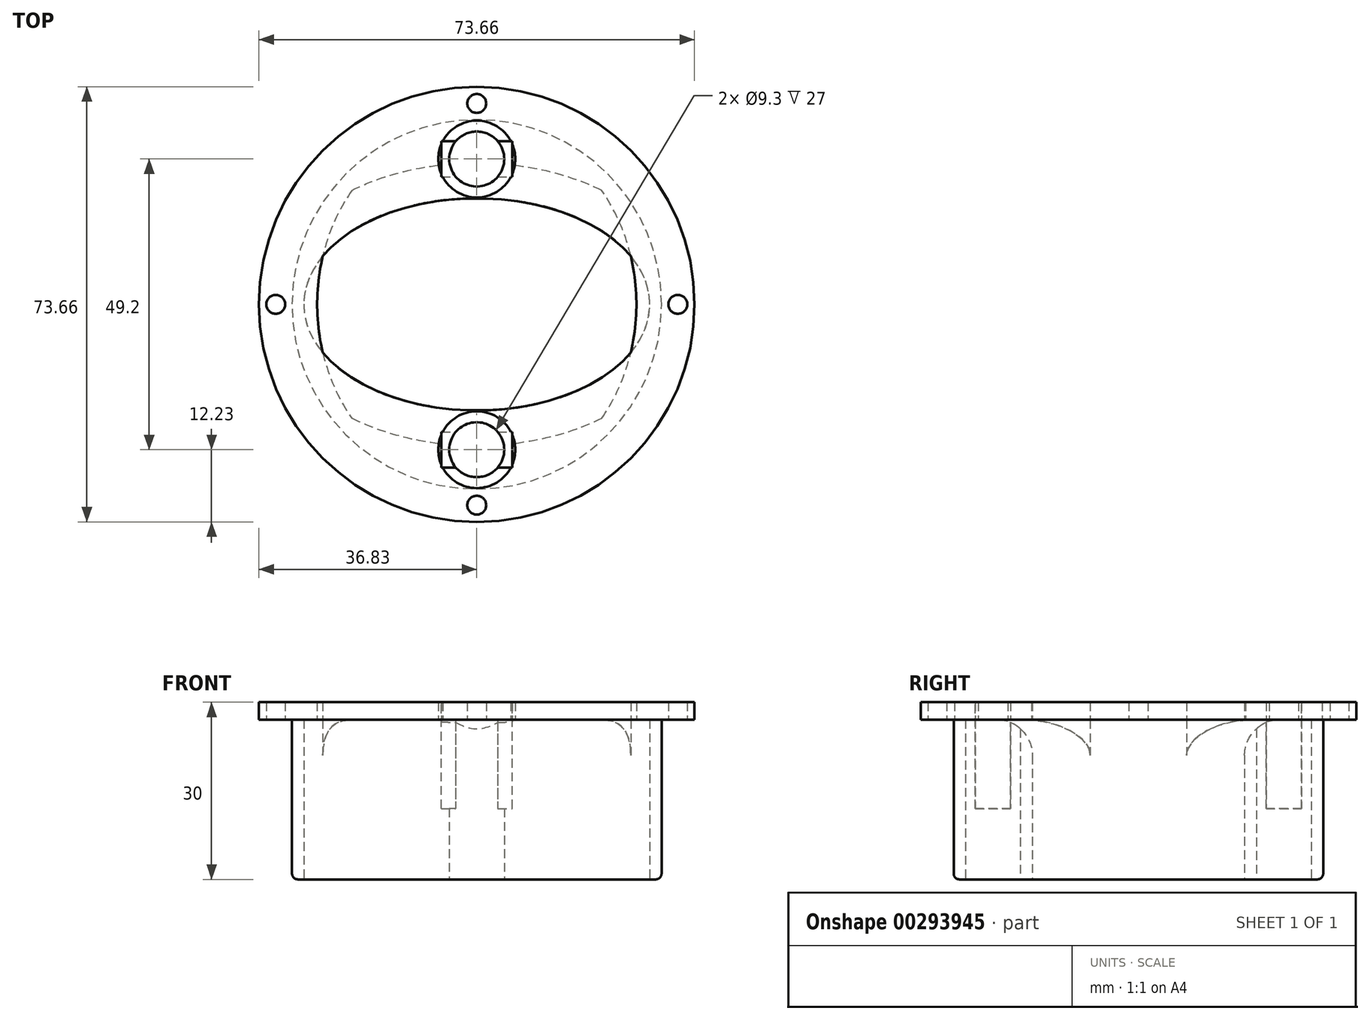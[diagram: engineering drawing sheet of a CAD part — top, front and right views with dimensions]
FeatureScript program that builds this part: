
annotation { "Feature Type Name" : "Feature", "Feature Type Description" : "" }
export const myFeature = defineFeature(function(context is Context, id is Id, definition is map)
    precondition{}
    {
        {
            var Q0;
            Q0=qCreatedBy(makeId("Top.planeOp"),FACE);
            var sketch = newSketch(context, id + "F0", { "sketchPlane" : qUnion([Q0])});
            skCircle(sketch, "E0", {"center": v(0, 0) * mm, "radius": 31.25 * mm});
            skCircle(sketch, "E1", {"center": v(0, 24.6) * mm, "radius": 4.65 * mm});
            skLineSegment(sketch, "E2", {"start": v(-31.25, 0) * mm, "end": v(31.25, 0) * mm, "construction": true});
            skCircle(sketch, "E3.MirrorC", {"center": v(0, -24.6) * mm, "radius": 4.65 * mm});
            skEllipse(sketch, "E4", {"center": v(0, 0) * mm, "majorRadius": 29.25 * mm, "minorRadius": 17.95 * mm, "majorAxis": v(-1, 0)});
            skPoint(sketch, "E5", {"position": v(0, 17.95) * mm});
            skPoint(sketch, "E6", {"position": v(0, -17.95) * mm});
            skPoint(sketch, "E7", {"position": v(29.25, 0) * mm});
            skSolve(sketch);
        }
        {
            var Q0;
            Q0 = qSketchRegion(id + "F0", true);
            extrude(context, id + "F1", {"entities" : qUnion([Q0]), "depth" : 27 * mm, "offsetDistance" : 25 * mm});
        }
        {
            var Q0;
            Q0=makeQuery(id+"F1.opExtrude","CAP_FACE",FACE,{"disambiguationData":[OSD([sQuery(id+"F0.wireOp",EDGE,"E0"),sQuery(id+"F0.wireOp",EDGE,"E1"),sQuery(id+"F0.wireOp",EDGE,"E3.MirrorC"),sQuery(id+"F0.wireOp",EDGE,"E4")])],"isStart":false});
            var sketch = newSketch(context, id + "F2", { "sketchPlane" : qUnion([Q0])});
            skCircle(sketch, "E8", {"center": v(0, 0) * mm, "radius": 36.83 * mm});
            skCircle(sketch, "E9", {"center": v(0, 34) * mm, "radius": 1.6 * mm});
            skCircle(sketch, "E10.1.0", {"center": v(-34, 0) * mm, "radius": 1.6 * mm});
            skCircle(sketch, "E10.2.0", {"center": v(0, -34) * mm, "radius": 1.6 * mm});
            skCircle(sketch, "E10.3.0", {"center": v(34, 0) * mm, "radius": 1.6 * mm});
            skEllipse(sketch, "E11", {"center": v(0, 0) * mm, "majorRadius": 31 * mm, "minorRadius": 27 * mm, "majorAxis": v(0, 1)});
            skPoint(sketch, "E12", {"position": v(-27, 0) * mm});
            skPoint(sketch, "E13", {"position": v(27, 0) * mm});
            skSolve(sketch);
        }
        {
            var Q0;
            Q0 = qSketchRegion(id + "F2", true);
            extrude(context, id + "F3", {"entities" : qUnion([Q0]), "operationType" : NewBodyOperationType.ADD, "depth" : 3 * mm, "offsetDistance" : 25 * mm});
        }
        {
            var Q0;
            {var subQ0=sQuery(id+"F0.wireOp",EDGE,"E4");Q0=makeQuery(id+"F3.boolean.opBoolean","SPLIT",EDGE,{"disambiguationData":[topologyDisambiguationEdgeConnected([makeQuery(id+"F1.opExtrude","SWEPT_FACE",FACE,{"disambiguationData":[OSD([subQ0])]}),makeQuery(id+"F3.opExtrude","CAP_FACE",FACE,{"disambiguationData":[OSD([sQuery(id+"F2.wireOp",EDGE,"E8"),sQuery(id+"F2.wireOp",EDGE,"E9"),sQuery(id+"F2.wireOp",EDGE,"E10.1.0"),sQuery(id+"F2.wireOp",EDGE,"E10.2.0"),sQuery(id+"F2.wireOp",EDGE,"E10.3.0"),sQuery(id+"F2.wireOp",EDGE,"E11")])],"isStart":true})]),OD(0.0)],"derivedFrom":makeQuery(id+"F1.opExtrude","CAP_EDGE",EDGE,{"disambiguationData":[OSD([subQ0])],"isStart":false})});}
            var Q1;
            {var subQ0=sQuery(id+"F0.wireOp",EDGE,"E4");Q1=makeQuery(id+"F3.boolean.opBoolean","SPLIT",EDGE,{"disambiguationData":[topologyDisambiguationEdgeConnected([makeQuery(id+"F1.opExtrude","SWEPT_FACE",FACE,{"disambiguationData":[OSD([subQ0])]}),makeQuery(id+"F3.opExtrude","CAP_FACE",FACE,{"disambiguationData":[OSD([sQuery(id+"F2.wireOp",EDGE,"E8"),sQuery(id+"F2.wireOp",EDGE,"E9"),sQuery(id+"F2.wireOp",EDGE,"E10.1.0"),sQuery(id+"F2.wireOp",EDGE,"E10.2.0"),sQuery(id+"F2.wireOp",EDGE,"E10.3.0"),sQuery(id+"F2.wireOp",EDGE,"E11")])],"isStart":true})]),OD(1.0)],"derivedFrom":makeQuery(id+"F1.opExtrude","CAP_EDGE",EDGE,{"disambiguationData":[OSD([subQ0])],"isStart":false})});}
            fillet(context, id + "F4", {"entities" : qUnion([Q0, Q1]), "tangentPropagation" : true, "radius" : 6 * mm, "defaultsChanged" : true, "vertexSettings" : [], "allowEdgeOverflow" : false});
        }
        {
            var Q0;
            {var subQ0=sQuery(id+"F0.wireOp",EDGE,"E3.MirrorC");var subQ2=sQuery(id+"F0.wireOp",EDGE,"E4");Q0=makeQuery(id+"F3.boolean.opBoolean","SPLIT",FACE,{"disambiguationData":[TD([makeQuery(id+"F1.opExtrude","SWEPT_FACE",FACE,{"disambiguationData":[OSD([subQ0])]})])],"derivedFrom":makeQuery(id+"F1.opExtrude","CAP_FACE",FACE,{"disambiguationData":[OSD([sQuery(id+"F0.wireOp",EDGE,"E0"),sQuery(id+"F0.wireOp",EDGE,"E1"),subQ0,subQ2])],"isStart":false})});}
            var sketch = newSketch(context, id + "F5", { "sketchPlane" : qUnion([Q0])});
            skEllipticalArc(sketch, "E14.0", {});
            skEllipticalArc(sketch, "E14.1", {});
            skEllipticalArc(sketch, "E14.2", {});
            skCircle(sketch, "E15", {"center": v(0, 24.6) * mm, "radius": 6.4 * mm});
            skCircle(sketch, "E16", {"center": v(0, -24.6) * mm, "radius": 6.4 * mm});
            skEllipticalArc(sketch, "E17.trimOffspring", {});
            const initialGuessF5  = {"E14.0": [0, 0, -1, 0, 0.02925, 0.01795, 0.4724535712676554, 2.669139082322136], "E14.1": [0, 0, 0, 1, 0.031, 0.027, 1.8374466509007625, 4.445738656278822], "E14.2": [0, 0, -1, 0, 0.02925, 0.01795, 3.614046224857449, 5.810731735911931], "E17.trimOffspring": [0, 0, 0, 1, 0.031, 0.027, 4.979039304490556, 1.3041460026890304]};
            skSetInitialGuess(sketch, initialGuessF5);
            skSolve(sketch);
        }
        {
            var Q0;
            Q0 = qSketchRegion(id + "F5", true);
            var Q1;
            Q1=makeQuery(id+"F3.opExtrude","CAP_FACE",FACE,{"disambiguationData":[OSD([sQuery(id+"F2.wireOp",EDGE,"E8"),sQuery(id+"F2.wireOp",EDGE,"E9"),sQuery(id+"F2.wireOp",EDGE,"E10.1.0"),sQuery(id+"F2.wireOp",EDGE,"E10.2.0"),sQuery(id+"F2.wireOp",EDGE,"E10.3.0"),sQuery(id+"F2.wireOp",EDGE,"E11")])],"isStart":false});
            extrude(context, id + "F6", {"entities" : qUnion([Q0]), "operationType" : NewBodyOperationType.ADD, "endBound" : BoundingType.UP_TO_SURFACE, "depth" : 25 * mm, "endBoundEntityFace" : qUnion([Q1]), "offsetDistance" : 25 * mm});
        }
        {
            var Q0;
            Q0=makeQuery(id+"F6.opExtrude","CAP_FACE",FACE,{"disambiguationData":[OSD([sQuery(id+"F5.wireOp",EDGE,"E14.2"),sQuery(id+"F5.wireOp",EDGE,"E17.trimOffspring")])],"isStart":true});
            var sketch = newSketch(context, id + "F7", { "sketchPlane" : qUnion([Q0])});
            skCircle(sketch, "E18", {"center": v(0, 24.6) * mm, "radius": 6.5 * mm});
            skCircle(sketch, "E19", {"center": v(0, -24.6) * mm, "radius": 6.5 * mm});
            skSolve(sketch);
        }
        {
            var Q0;
            Q0 = qSketchRegion(id + "F7", true);
            extrude(context, id + "F8", {"entities" : qUnion([Q0]), "operationType" : NewBodyOperationType.REMOVE, "endBound" : BoundingType.THROUGH_ALL, "oppositeDirection" : true, "depth" : 25 * mm, "offsetDistance" : 25 * mm});
        }
        {
            var Q0;
            Q0=makeQuery(id+"F1.opExtrude","CAP_EDGE",EDGE,{"disambiguationData":[OSD([sQuery(id+"F0.wireOp",EDGE,"E0")])],"isStart":true});
            fillet(context, id + "F9", {"entities" : qUnion([Q0]), "tangentPropagation" : true, "radius" : 1 * mm, "defaultsChanged" : true, "vertexSettings" : [], "allowEdgeOverflow" : false});
        }
        {
            var Q0;
            Q0=makeQuery(id+"F6.boolean.opBoolean","MERGE",FACE,{"derivedFrom":[makeQuery(id+"F3.opExtrude","CAP_FACE",FACE,{"disambiguationData":[OSD([sQuery(id+"F2.wireOp",EDGE,"E8"),sQuery(id+"F2.wireOp",EDGE,"E9"),sQuery(id+"F2.wireOp",EDGE,"E10.1.0"),sQuery(id+"F2.wireOp",EDGE,"E10.2.0"),sQuery(id+"F2.wireOp",EDGE,"E10.3.0"),sQuery(id+"F2.wireOp",EDGE,"E11")])],"isStart":false}),makeQuery(id+"F6.opExtrude","CAP_FACE",FACE,{"disambiguationData":[OSD([sQuery(id+"F5.wireOp",EDGE,"E14.0"),sQuery(id+"F5.wireOp",EDGE,"E14.1")])],"isStart":false}),makeQuery(id+"F6.opExtrude","CAP_FACE",FACE,{"disambiguationData":[OSD([sQuery(id+"F5.wireOp",EDGE,"E14.2"),sQuery(id+"F5.wireOp",EDGE,"E17.trimOffspring")])],"isStart":false})]});
            var sketch = newSketch(context, id + "F10", { "sketchPlane" : qUnion([Q0])});
            skLineSegment(sketch, "E20.bottom", {"start": v(-6, 21.6) * mm, "end": v(6, 21.6) * mm});
            skLineSegment(sketch, "E20.top", {"start": v(-6, 27.6) * mm, "end": v(6, 27.6) * mm});
            skLineSegment(sketch, "E20.left", {"start": v(-6, 21.6) * mm, "end": v(-6, 27.6) * mm});
            skLineSegment(sketch, "E20.right", {"start": v(6, 21.6) * mm, "end": v(6, 27.6) * mm});
            skPoint(sketch, "E20.middle", {"position": v(0, 24.6) * mm});
            skLineSegment(sketch, "E21.bottom", {"start": v(-6, -27.6) * mm, "end": v(6, -27.6) * mm});
            skLineSegment(sketch, "E21.top", {"start": v(-6, -21.6) * mm, "end": v(6, -21.6) * mm});
            skLineSegment(sketch, "E21.left", {"start": v(-6, -27.6) * mm, "end": v(-6, -21.6) * mm});
            skLineSegment(sketch, "E21.right", {"start": v(6, -27.6) * mm, "end": v(6, -21.6) * mm});
            skPoint(sketch, "E21.middle", {"position": v(0, -24.6) * mm});
            skSolve(sketch);
        }
        {
            var Q0;
            Q0 = qSketchRegion(id + "F10", true);
            extrude(context, id + "F11", {"entities" : qUnion([Q0]), "operationType" : NewBodyOperationType.REMOVE, "oppositeDirection" : true, "depth" : 18 * mm, "offsetDistance" : 25 * mm});
        }
    });
